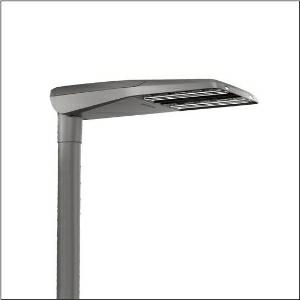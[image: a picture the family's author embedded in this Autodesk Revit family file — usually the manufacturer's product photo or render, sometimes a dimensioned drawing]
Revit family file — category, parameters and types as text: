
# Revit family: streetlight_sl_11_iq_midi___st1_2p1_0_5xc3g41e08me_f4ca
name_source: partatom
category: Lighting Fixtures
units: mm (PartAtom-declared; Revit-internal decimal feet)

## family parameters
Cut with Voids When Loaded = No
Host = Face
Light Source = No
Part Type = Normal
Room Calculation Point = No
Round Connector Dimension = Use Diameter
Shared = No

## types (1)
- --- (1 x LED, 18520 lm, 121.7 W, 4000K)
    Apparent Load = 122 VA
    CIE Flux Codes = 31 68 95 100 100
    Color Rendering = 70
    Color Temperature = 4000K
    Default Elevation = 1800 mm
    Description = Streetlight SL 11 iQ midi, mast luminaire, primary light control with 3 zone facetted reflector, of plastic, silver coated, highly specular, primary optical cover: cover, of PMMA, transparent, light distribution: ST1.2P1.0, light emission: direct distribution, primary light characteristic: asymmetric, installation type: post-top, side-entry, lamps: LED, High Power LED, rated values: 18.520lm | 121,7W | 152,2lm/W (begin service life); end service life: 18.520lm | 129W; at 50% lumin. flux: 9.260lm | 56,2W | 164,8lm/W, colour temperature: 4000K, colour rendering: CRI > 70, light colour: 740, light setting 1 begin service life: 100% | 18.520lm | 121,7W | 152,2lm/W | 4.000K, light setting 1 end service life: 129W, further light settings possible, control: optimised constant luminous flux control (CLO 2.0), Desk-Remote (wireless, voltage-free reading and setting of iQ features in the workshop via application-optimized NFC function/RFID function), Light-Fading, Smart-Wire, Night-Set, Lumen-Switch, Temp-Guard, Auto-Match, with cable H07RN-F 3x 1.5mm², mains connection: 230..240V, AC, 50/60Hz, connection cable pre-assembled, cable length: 12,5m, luminaire housing, of diecast aluminium, powder-coated, SITECO metallic grey (DB 702S), please order mast flange separately, inclination adjustable without tools: 0°, 5°, 10°, 15° (post-top) | 0°, -5°, -10°, -15° (side-entry), sealing non-destructively replaceable, multi-level sealing system, length: 780mm, width: 376mm, height: 118mm, mast flange for spigot size: 42mm (side-entry): 5XC10008XM4, 60/48mm (side-entry/post-top): 5XC10108XM2, 76/60mm (side-entry/post-top): 5XC10108XM1, equipment: Power, protection rating (complete): IP66, insulation class (complete): insulation class II (safety insulation), certification: CE, ENEC, ENEC+, VDE, impact resistance: IK10, permissible operating ambient temperature for outdoor applications: -25..+50°C, standard-compliant lighting for roads and squares, Environmental Product Declaration (EPD) tested and certified by an independent institute, packaging unit: 1 piece

Light Distribution: ST1.2P1.0
    Height = 118 mm
    Lamp = 1 x LED
    Lamp Light Flux = 18520 lm
    Lamp Power = 121.7 W
    Lamp count = 1
    Length = 780 mm
    Luminous efficacy = 152 lm/W
    Manufacturer = Siteco
    ModVariant = No
    Model = 5XC3G41E08ME
    Number of Poles = 1
    OnlyDefault = Yes
    Power Factor = 1
    Product Name = Streetlight SL 11 iQ midi | ST1.2P1.0
    Product group = mast luminaire | pylon top
    ProductGroupID = 6100
    Protection Class = Protection class II
    Protection Degree = IP 66
    RLX_Detail_Level = 1
    RLX_Emergency_Light_Flux = 0 lm
    RLX_Emergency_Type = 0
    RLX_Emergency_Type_DB = No
    RlxData = <blob elided: 70957 chars, md5=48828dd9>
    Socket = socket
    Standby Power = 0 W
    System Light Flux = 18520 lm
    System Power = 122 W
    Type Comments = factory setting: luminous flux: 100 % | dim-lin: 254 | 544 mA
    Type Image = l_1005960.jpg
    URL = http://relux.com
    VarID = @adj_044245
    Voltage = 0 V
    Weight = 0.00 kg
    Width = 376 mm

## geometry (parser evidence)
native form markers: Blend x4, Sweep x9
no freeform markers — native parametric forms only
